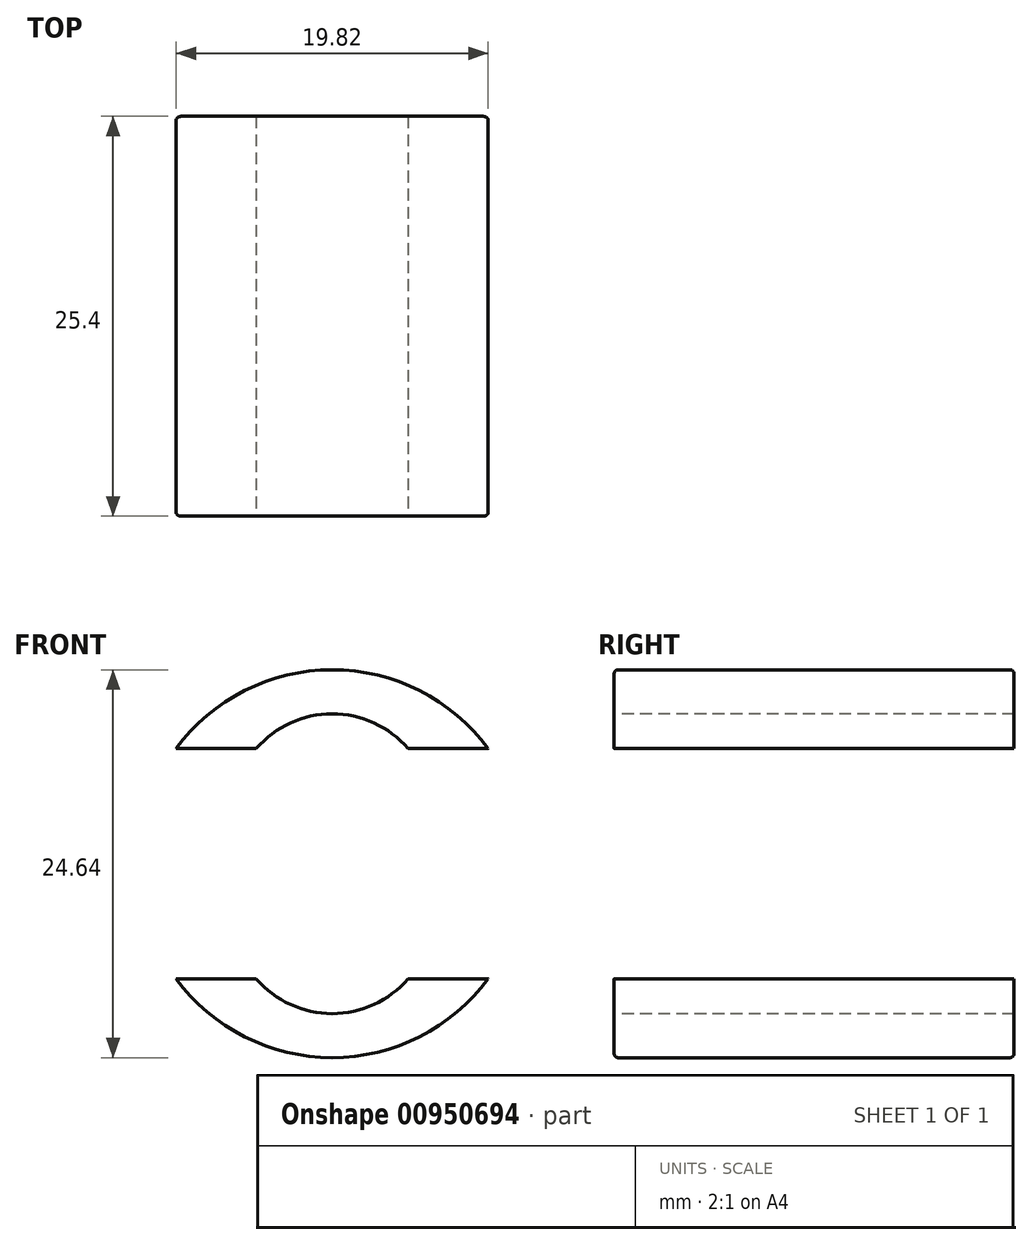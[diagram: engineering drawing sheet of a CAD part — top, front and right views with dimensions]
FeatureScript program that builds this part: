
annotation { "Feature Type Name" : "Feature", "Feature Type Description" : "" }
export const myFeature = defineFeature(function(context is Context, id is Id, definition is map)
    precondition{}
    {
        {
            var Q0;
            Q0=qCreatedBy(makeId("Front.planeOp"),FACE);
            var sketch = newSketch(context, id + "F0", { "sketchPlane" : qUnion([Q0])});
            skCircle(sketch, "E0", {"center": v(0, 0) * mm, "radius": 12.32 * mm});
            skSolve(sketch);
        }
        {
            var Q0;
            Q0=qSketchRegion(id+"F0",true);
            extrude(context, id + "F1", {"entities" : qUnion([Q0]), "depth" : 25.4 * mm, "offsetDistance" : 25.4 * mm});
        }
        {
            var Q0;
            Q0=makeQuery(id+"F1.opExtrude","CAP_FACE",FACE,{"disambiguationData":[OSD([sQuery(id+"F0.wireOp",EDGE,"E0")])],"isStart":false});
            var sketch = newSketch(context, id + "F2", { "sketchPlane" : qUnion([Q0])});
            skPoint(sketch, "E1.middle", {"position": v(0, 0) * mm});
            skArc(sketch, "E2", {"start": v(9.91, 7.31) * mm, "mid": v(0, 12.32) * mm, "end": v(-9.91, 7.31) * mm});
            skArc(sketch, "E3", {"start": v(4.82, 7.31) * mm, "mid": v(0, 9.53) * mm, "end": v(-4.82, 7.31) * mm});
            skLineSegment(sketch, "E4", {"start": v(-9.91, 7.31) * mm, "end": v(-4.82, 7.31) * mm});
            skLineSegment(sketch, "E5.trimOffspring", {"start": v(4.82, 7.31) * mm, "end": v(9.91, 7.31) * mm});
            skSolve(sketch);
        }
        {
            var Q0;
            Q0=qSketchRegion(id+"F2",true);
            extrude(context, id + "F3", {"entities" : qUnion([Q0]), "operationType" : NewBodyOperationType.INTERSECT, "oppositeDirection" : true, "depth" : 25.4 * mm, "offsetDistance" : 25.4 * mm});
        }
        {
            var Q0;
            Q0=makeQuery(id+"F1.opExtrude","SWEPT_BODY",BODY,{"disambiguationData":[OSD([sQuery(id+"F0.wireOp",EDGE,"E0")])]});
            var Q1;
            Q1=qCreatedBy(makeId("Top.planeOp"),FACE);
            mirror(context, id + "F4", {"entities" : qUnion([Q0]), "mirrorPlane" : qUnion([Q1])});
        }
        {
            var Q0;
            Q0=makeQuery(id+"F1.opExtrude","CAP_EDGE",EDGE,{"disambiguationData":[OSD([sQuery(id+"F0.wireOp",EDGE,"E0")])],"isStart":false});
            var Q1;
            Q1=makeQuery(id+"F1.opExtrude","CAP_EDGE",EDGE,{"disambiguationData":[OSD([sQuery(id+"F0.wireOp",EDGE,"E0")])],"isStart":true});
            var Q2;
            Q2=makeQuery(id+"F4.opPattern","COPY",EDGE,{"derivedFrom":makeQuery(id+"F1.opExtrude","CAP_EDGE",EDGE,{"disambiguationData":[OSD([sQuery(id+"F0.wireOp",EDGE,"E0")])],"isStart":false}),"instanceName":"1"});
            var Q3;
            Q3=makeQuery(id+"F4.opPattern","COPY",EDGE,{"derivedFrom":makeQuery(id+"F1.opExtrude","CAP_EDGE",EDGE,{"disambiguationData":[OSD([sQuery(id+"F0.wireOp",EDGE,"E0")])],"isStart":true}),"instanceName":"1"});
            fillet(context, id + "F5", {"entities" : qUnion([Q0, Q1, Q2, Q3]), "radius" : 0.25 * mm, "tangentPropagation" : true, "allowEdgeOverflow" : false});
        }
    });
